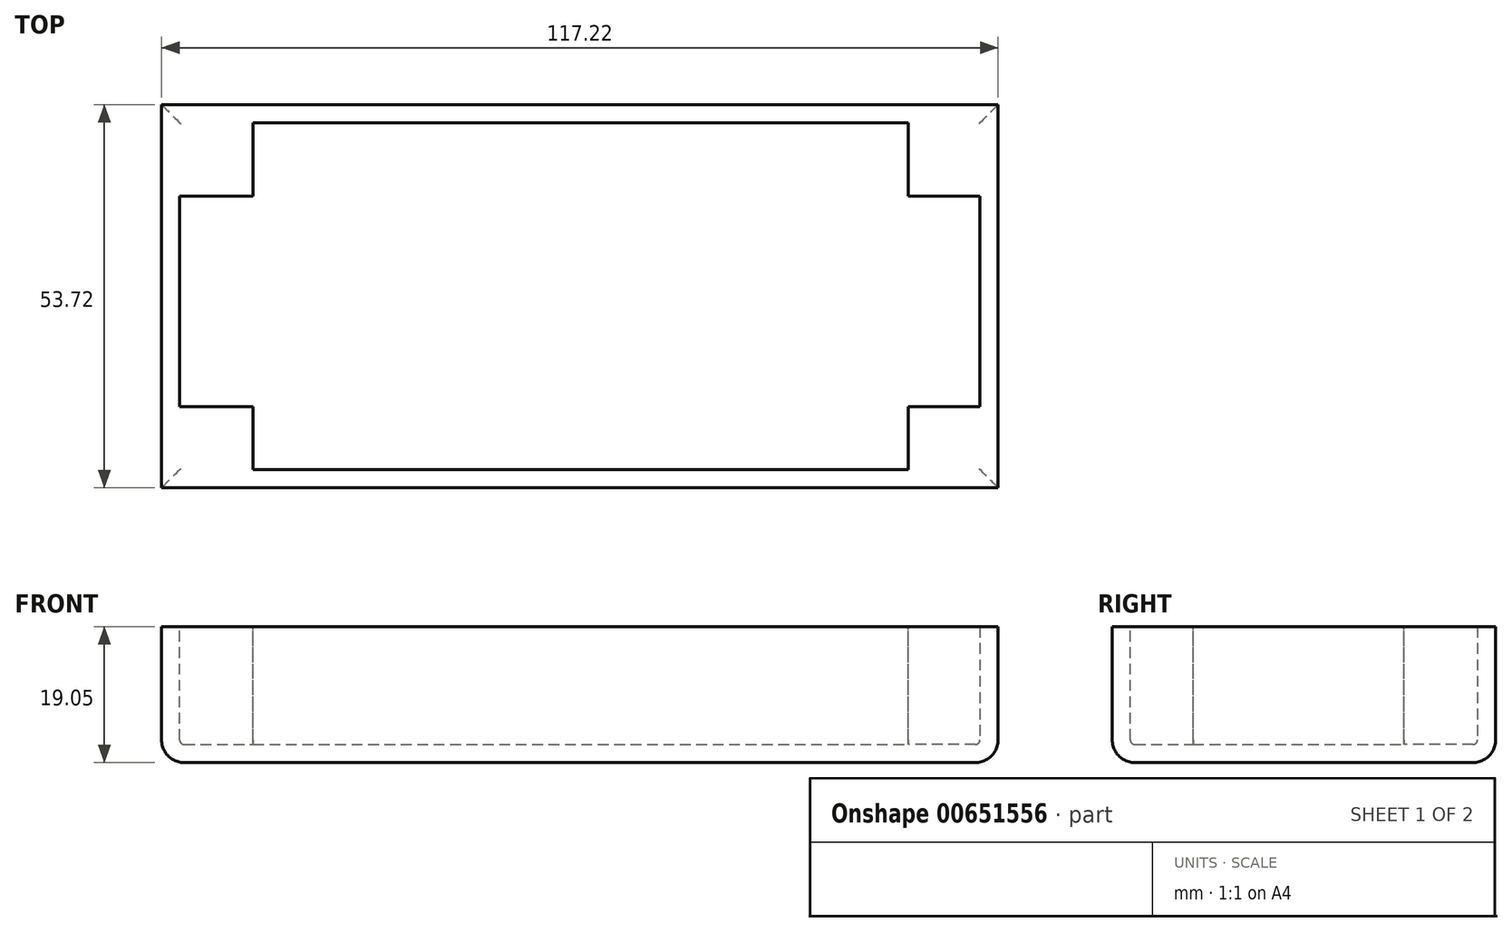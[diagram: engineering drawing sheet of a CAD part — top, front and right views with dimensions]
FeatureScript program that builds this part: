
annotation { "Feature Type Name" : "Feature", "Feature Type Description" : "" }
export const myFeature = defineFeature(function(context is Context, id is Id, definition is map)
    precondition{}
    {
        {
            var Q0;
            Q0=qCreatedBy(makeId("Top.planeOp"),FACE);
            var sketch = newSketch(context, id + "F0", { "sketchPlane" : qUnion([Q0])});
            skLineSegment(sketch, "E0.0", {"start": v(-58.61, -26.86) * mm, "end": v(-58.61, 26.86) * mm});
            skLineSegment(sketch, "E0.1", {"start": v(58.61, -26.86) * mm, "end": v(-58.61, -26.86) * mm});
            skLineSegment(sketch, "E0.2", {"start": v(58.61, -26.86) * mm, "end": v(58.61, 26.86) * mm});
            skLineSegment(sketch, "E0.3", {"start": v(58.61, 26.86) * mm, "end": v(-58.61, 26.86) * mm});
            skSolve(sketch);
        }
        {
            var Q0;
            Q0=makeQuery(id+"F0.imprint","IMPRINT",FACE,{"disambiguationData":[TD([[makeQuery(id+"F0.imprint","IMPRINT",EDGE,{"derivedFrom":sQuery(id+"F0.wireOp",EDGE,"843f9caf-4b0b-4388-9948-a010be600218.bottom")}),-1.0]])]});
            var Q1;
            Q1=makeQuery(id+"F0.imprint","IMPRINT",FACE,{"disambiguationData":[TD([[makeQuery(id+"F0.imprint","IMPRINT",EDGE,{"derivedFrom":sQuery(id+"F0.wireOp",EDGE,"E0.0")}),-1.0]])]});
            extrude(context, id + "F1", {"entities" : qUnion([Q0, Q1]), "depth" : 19.05 * mm, "offsetDistance" : 25.4 * mm});
        }
        {
            var Q0;
            Q0=makeQuery(id+"F1.opExtrude","CAP_FACE",FACE,{"disambiguationData":[OSD([sQuery(id+"F0.wireOp",EDGE,"843f9caf-4b0b-4388-9948-a010be600218.bottom"),sQuery(id+"F0.wireOp",EDGE,"843f9caf-4b0b-4388-9948-a010be600218.top"),sQuery(id+"F0.wireOp",EDGE,"843f9caf-4b0b-4388-9948-a010be600218.left"),sQuery(id+"F0.wireOp",EDGE,"843f9caf-4b0b-4388-9948-a010be600218.right")])],"isStart":true});
            var Q1;
            Q1=makeQuery(id+"F1.opExtrude","CAP_EDGE",EDGE,{"disambiguationData":[OSD([sQuery(id+"F0.wireOp",EDGE,"E0.1")])],"isStart":true});
            var Q2;
            Q2=makeQuery(id+"F1.opExtrude","CAP_EDGE",EDGE,{"disambiguationData":[OSD([sQuery(id+"F0.wireOp",EDGE,"E0.0")])],"isStart":true});
            var Q3;
            Q3=makeQuery(id+"F1.opExtrude","CAP_EDGE",EDGE,{"disambiguationData":[OSD([sQuery(id+"F0.wireOp",EDGE,"E0.3")])],"isStart":true});
            var Q4;
            Q4=makeQuery(id+"F1.opExtrude","CAP_EDGE",EDGE,{"disambiguationData":[OSD([sQuery(id+"F0.wireOp",EDGE,"E0.2")])],"isStart":true});
            fillet(context, id + "F2", {"entities" : qUnion([Q0, Q1, Q2, Q3, Q4]), "radius" : 3.17 * mm, "tangentPropagation" : true, "allowEdgeOverflow" : false});
        }
        {
            var Q0;
            Q0=makeQuery(id+"F1.opExtrude","CAP_FACE",FACE,{"disambiguationData":[OSD([sQuery(id+"F0.wireOp",EDGE,"843f9caf-4b0b-4388-9948-a010be600218.bottom"),sQuery(id+"F0.wireOp",EDGE,"843f9caf-4b0b-4388-9948-a010be600218.top"),sQuery(id+"F0.wireOp",EDGE,"843f9caf-4b0b-4388-9948-a010be600218.left"),sQuery(id+"F0.wireOp",EDGE,"843f9caf-4b0b-4388-9948-a010be600218.right")])],"isStart":false});
            var Q1;
            Q1=makeQuery(id+"F1.opExtrude","CAP_FACE",FACE,{"disambiguationData":[OSD([sQuery(id+"F0.wireOp",EDGE,"E0.0"),sQuery(id+"F0.wireOp",EDGE,"E0.1"),sQuery(id+"F0.wireOp",EDGE,"E0.2"),sQuery(id+"F0.wireOp",EDGE,"E0.3")])],"isStart":false});
            shell(context, id + "F3", {"entities" : qUnion([Q0, Q1]), "thickness" : 2.54 * mm});
        }
        {
            var Q0;
            Q0=qCreatedBy(makeId("Top.planeOp"),FACE);
            cPlane(context, id + "F4", {"entities" : qUnion([Q0]), "cplaneType" : CPlaneType.OFFSET, "offset" : 19.05 * mm, "width" : 152.4 * mm, "height" : 152.4 * mm});
        }
        {
            var Q0;
            Q0=qCreatedBy(id+"F4.planeOp",FACE);
            var sketch = newSketch(context, id + "F5", { "sketchPlane" : qUnion([Q0])});
            skLineSegment(sketch, "E1.bottom", {"start": v(58.2, 26.2) * mm, "end": v(46, 26.2) * mm});
            skLineSegment(sketch, "E1.top", {"start": v(57.7, 14) * mm, "end": v(46, 14) * mm});
            skLineSegment(sketch, "E1.right", {"start": v(46, 26.2) * mm, "end": v(46, 14) * mm});
            skLineSegment(sketch, "E2", {"start": v(57.7, -30.19) * mm, "end": v(-62.7, 26.7) * mm, "construction": true});
            skLineSegment(sketch, "E3", {"start": v(-62.7, -30.19) * mm, "end": v(57.7, 26.67) * mm, "construction": true});
            skLineSegment(sketch, "E4", {"start": v(-2.48, -1.75) * mm, "end": v(96.78, -1.75) * mm, "construction": true});
            skLineSegment(sketch, "E5", {"start": v(-2.48, -1.75) * mm, "end": v(-2.48, 68.2) * mm, "construction": true});
            skLineSegment(sketch, "E6.MirrorCS", {"start": v(-57.03, 14) * mm, "end": v(-45.78, 14) * mm});
            skLineSegment(sketch, "E7.MirrorCS", {"start": v(-45.78, 26.2) * mm, "end": v(-45.78, 14) * mm});
            skLineSegment(sketch, "E8.MirrorCS", {"start": v(-57.03, 26.2) * mm, "end": v(-45.78, 26.2) * mm});
            skLineSegment(sketch, "E9.MirrorCS", {"start": v(57.7, -15.52) * mm, "end": v(46, -15.52) * mm});
            skLineSegment(sketch, "E10.MirrorCS", {"start": v(46, -25.35) * mm, "end": v(46, -15.52) * mm});
            skLineSegment(sketch, "E11.MirrorCS", {"start": v(-57.03, -15.52) * mm, "end": v(-45.78, -15.52) * mm});
            skLineSegment(sketch, "E12.MirrorCS", {"start": v(-45.78, -25.35) * mm, "end": v(-45.78, -15.52) * mm});
            skLineSegment(sketch, "E13", {"start": v(-57.03, 26.2) * mm, "end": v(-57.03, 14) * mm});
            skPoint(sketch, "E13.endSnap0", {"position": v(-51.87, -27.71) * mm});
            skLineSegment(sketch, "E14", {"start": v(-57.03, -25.35) * mm, "end": v(-45.78, -25.35) * mm});
            skLineSegment(sketch, "E15", {"start": v(57.7, -25.35) * mm, "end": v(57.7, -15.52) * mm});
            skLineSegment(sketch, "E16.trimOffspring", {"start": v(57.7, 14) * mm, "end": v(57.7, 26.2) * mm});
            skPoint(sketch, "E17.orphan", {"position": v(57.7, -27.71) * mm});
            skLineSegment(sketch, "E18.trimOffspring", {"start": v(46, -25.35) * mm, "end": v(57.7, -25.35) * mm});
            skPoint(sketch, "E19.orphan", {"position": v(-45.78, -27.71) * mm});
            skPoint(sketch, "E20.orphan", {"position": v(-57.97, -27.71) * mm});
            skPoint(sketch, "E21.trimOffspring.end.orphan", {"position": v(-57.03, -27.71) * mm});
            skLineSegment(sketch, "E22.trimOffspring", {"start": v(-57.03, -15.52) * mm, "end": v(-57.03, -25.35) * mm});
            skSolve(sketch);
        }
        {
            var Q0;
            Q0=makeQuery(id+"F5.imprint","IMPRINT",FACE,{"disambiguationData":[TD([[makeQuery(id+"F5.imprint","IMPRINT",EDGE,{"derivedFrom":sQuery(id+"F5.wireOp",EDGE,"a087a1b8-f9da-475a-b3bc-d167547f6ca6.MirrorCS")}),1.0]])]});
            var Q1;
            Q1=makeQuery(id+"F5.imprint","IMPRINT",FACE,{"disambiguationData":[TD([[makeQuery(id+"F5.imprint","IMPRINT",EDGE,{"derivedFrom":sQuery(id+"F5.wireOp",EDGE,"E11.MirrorCS")}),-1.0]])]});
            var Q2;
            Q2=makeQuery(id+"F5.imprint","IMPRINT",FACE,{"disambiguationData":[TD([[makeQuery(id+"F5.imprint","IMPRINT",EDGE,{"derivedFrom":sQuery(id+"F5.wireOp",EDGE,"cda294fc-eb7e-4b44-bf46-7c3afe327d31.MirrorCS")}),1.0]])]});
            var Q3;
            Q3=makeQuery(id+"F5.imprint","IMPRINT",FACE,{"disambiguationData":[TD([[makeQuery(id+"F5.imprint","IMPRINT",EDGE,{"derivedFrom":sQuery(id+"F5.wireOp",EDGE,"E1.bottom")}),1.0]])]});
            var Q4;
            Q4=makeQuery(id+"F5.imprint","IMPRINT",FACE,{"disambiguationData":[TD([[makeQuery(id+"F5.imprint","IMPRINT",EDGE,{"derivedFrom":sQuery(id+"F5.wireOp",EDGE,"E6.MirrorCS")}),1.0]])]});
            var Q5;
            Q5=makeQuery(id+"F5.imprint","IMPRINT",FACE,{"disambiguationData":[TD([[makeQuery(id+"F5.imprint","IMPRINT",EDGE,{"derivedFrom":sQuery(id+"F5.wireOp",EDGE,"E9.MirrorCS")}),1.0]])]});
            extrude(context, id + "F6", {"entities" : qUnion([Q0, Q1, Q2, Q3, Q4, Q5]), "operationType" : NewBodyOperationType.ADD, "oppositeDirection" : true, "depth" : 17.78 * mm, "offsetDistance" : 25.4 * mm});
        }
    });
